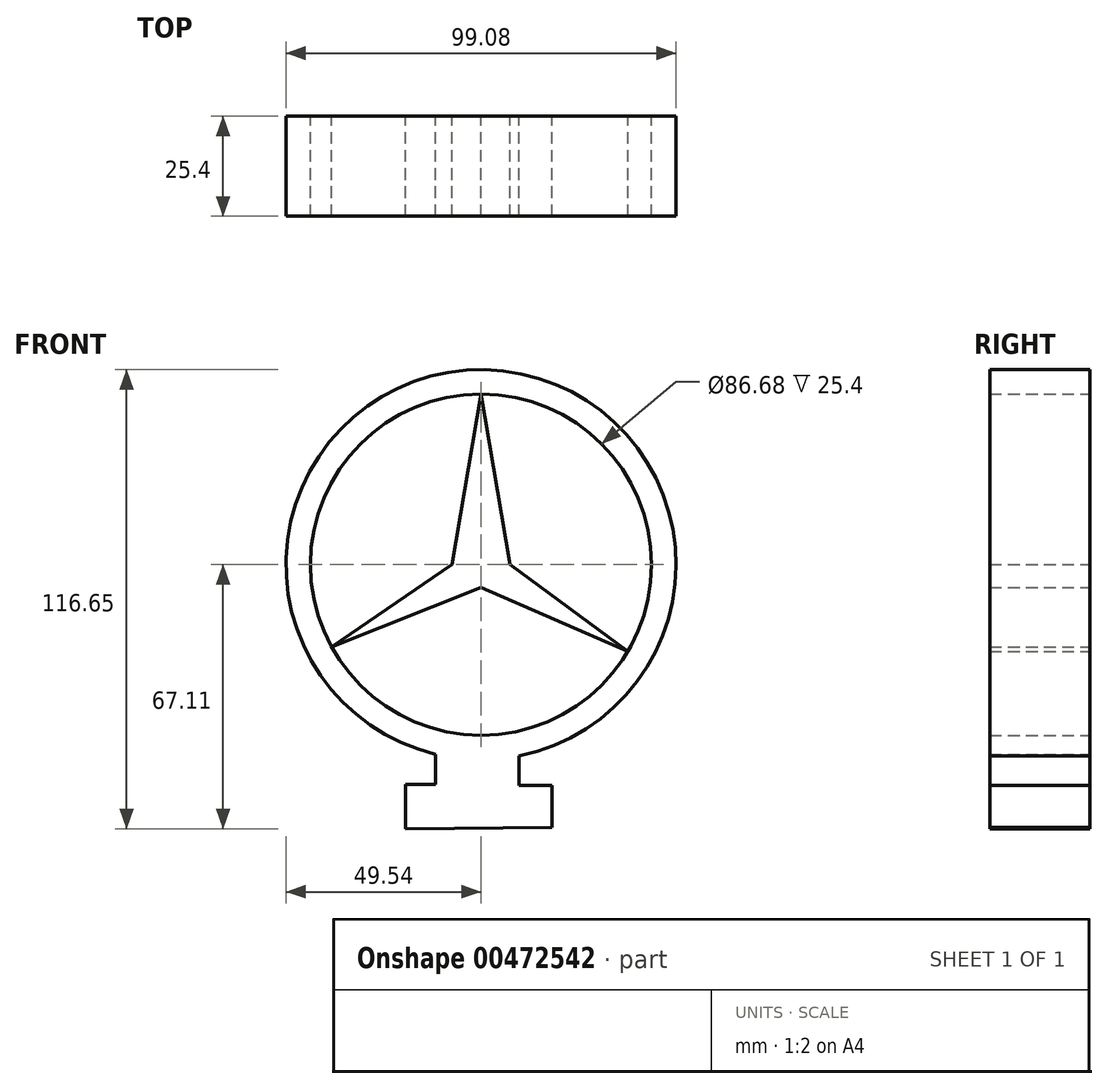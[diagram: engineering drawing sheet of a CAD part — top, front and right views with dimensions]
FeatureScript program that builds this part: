
annotation { "Feature Type Name" : "Feature", "Feature Type Description" : "" }
export const myFeature = defineFeature(function(context is Context, id is Id, definition is map)
    precondition{}
    {
        {
            var Q0;
            Q0=qCreatedBy(makeId("Front.planeOp"),FACE);
            var sketch = newSketch(context, id + "F0", { "sketchPlane" : qUnion([Q0])});
            skCircle(sketch, "E0", {"center": v(0, 0) * mm, "radius": 43.34 * mm});
            skLineSegment(sketch, "E1", {"start": v(-7.33, 0) * mm, "end": v(0, 43.34) * mm});
            skLineSegment(sketch, "E2", {"start": v(7.33, 0) * mm, "end": v(0, 43.34) * mm});
            skLineSegment(sketch, "E3", {"start": v(-7.33, 0) * mm, "end": v(-37.98, -20.88) * mm});
            skLineSegment(sketch, "E4", {"start": v(7.33, 0) * mm, "end": v(37.33, -22.01) * mm});
            skLineSegment(sketch, "E5", {"start": v(-37.98, -20.88) * mm, "end": v(0, -5.75) * mm});
            skLineSegment(sketch, "E6", {"start": v(37.33, -22.01) * mm, "end": v(0, -5.75) * mm});
            skLineSegment(sketch, "E7", {"start": v(-19.23, -55.82) * mm, "end": v(18.03, -56.12) * mm});
            skLineSegment(sketch, "E8", {"start": v(-19.23, -55.82) * mm, "end": v(-19.23, -67.11) * mm});
            skLineSegment(sketch, "E9", {"start": v(18.03, -56.12) * mm, "end": v(18.03, -66.8) * mm});
            skLineSegment(sketch, "E10", {"start": v(-19.23, -67.11) * mm, "end": v(18.03, -66.8) * mm});
            skLineSegment(sketch, "E11", {"start": v(0.53, 40.21) * mm, "end": v(0, 0) * mm});
            skLineSegment(sketch, "E12", {"start": v(0, 0) * mm, "end": v(-37.98, -20.88) * mm});
            skLineSegment(sketch, "E13", {"start": v(37.33, -22.01) * mm, "end": v(-1.24, -0.68) * mm});
            skCircle(sketch, "E14", {"center": v(0, 0) * mm, "radius": 49.54 * mm});
            skLineSegment(sketch, "E15", {"start": v(-11.52, -48.18) * mm, "end": v(-11.52, -55.88) * mm});
            skLineSegment(sketch, "E16", {"start": v(9.65, -48.6) * mm, "end": v(9.65, -56.05) * mm});
            skSolve(sketch);
        }
        {
            var Q0;
            {var subQ4=sQuery(id+"F0.wireOp",EDGE,"E14");var subQ5=makeQuery(id+"F0.imprint","INTERSECT",VERTEX,{"derivedFrom":[subQ4,sQuery(id+"F0.wireOp",EDGE,"E15")]});Q0=makeQuery(id+"F0.imprint","IMPRINT",FACE,{"disambiguationData":[TD([[makeQuery(id+"F0.imprint","IMPRINT",EDGE,{"disambiguationData":[TD([[subQ5,-1.0]])],"derivedFrom":subQ4}),1.0]])]});}
            var Q1;
            {var subQ2=sQuery(id+"F0.wireOp",EDGE,"E1");Q1=makeQuery(id+"F0.imprint","IMPRINT",FACE,{"disambiguationData":[TD([[makeQuery(id+"F0.imprint","IMPRINT",EDGE,{"derivedFrom":subQ2}),-1.0]])]});}
            var Q2;
            {var subQ3=sQuery(id+"F0.wireOp",EDGE,"E4");Q2=makeQuery(id+"F0.imprint","IMPRINT",FACE,{"disambiguationData":[TD([[makeQuery(id+"F0.imprint","IMPRINT",EDGE,{"derivedFrom":subQ3}),-1.0]])]});}
            var Q3;
            {var subQ0=sQuery(id+"F0.wireOp",EDGE,"E5");Q3=makeQuery(id+"F0.imprint","IMPRINT",FACE,{"disambiguationData":[TD([[makeQuery(id+"F0.imprint","IMPRINT",EDGE,{"derivedFrom":subQ0}),1.0]])]});}
            var Q4;
            {var subQ0=sQuery(id+"F0.wireOp",EDGE,"E15");Q4=makeQuery(id+"F0.imprint","IMPRINT",FACE,{"disambiguationData":[TD([[makeQuery(id+"F0.imprint","IMPRINT",EDGE,{"derivedFrom":subQ0}),1.0]])]});}
            var Q5;
            {var subQ0=sQuery(id+"F0.wireOp",EDGE,"E8");Q5=makeQuery(id+"F0.imprint","IMPRINT",FACE,{"disambiguationData":[TD([[makeQuery(id+"F0.imprint","IMPRINT",EDGE,{"derivedFrom":subQ0}),1.0]])]});}
            extrude(context, id + "F1", {"entities" : qUnion([Q0, Q1, Q2, Q3, Q4, Q5]), "depth" : 25.4 * mm});
        }
    });
